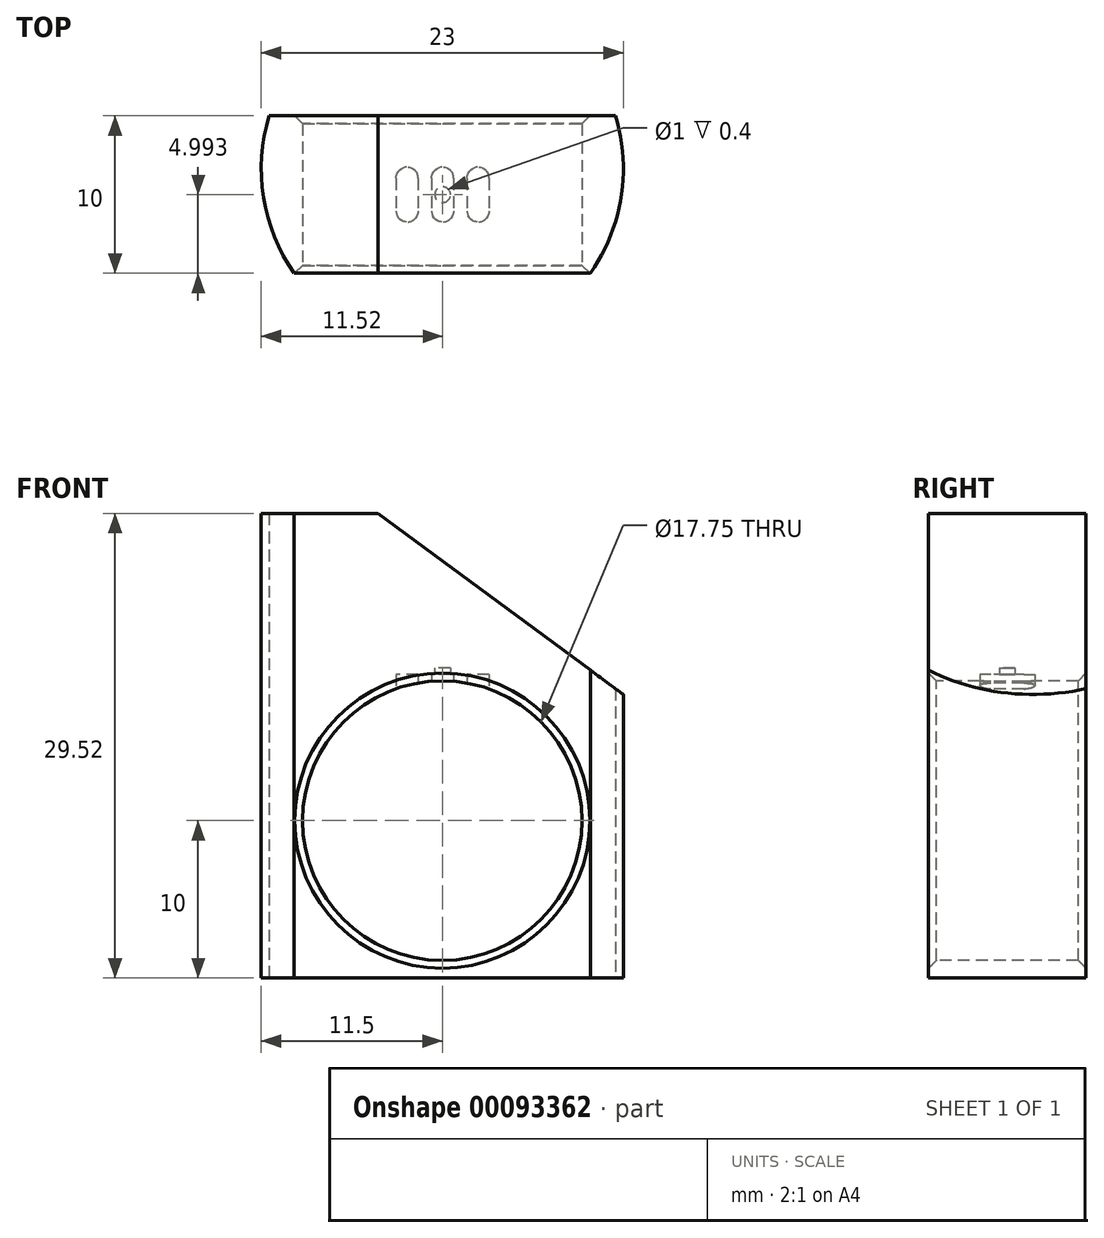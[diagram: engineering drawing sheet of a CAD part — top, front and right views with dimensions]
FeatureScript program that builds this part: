
annotation { "Feature Type Name" : "Feature", "Feature Type Description" : "" }
export const myFeature = defineFeature(function(context is Context, id is Id, definition is map)
    precondition{}
    {
        {
            var Q0;
            Q0=qCreatedBy(makeId("Front.planeOp"),FACE);
            var sketch = newSketch(context, id + "F0", { "sketchPlane" : qUnion([Q0])});
            skCircle(sketch, "E0", {"center": v(0, 0) * mm, "radius": 8.88 * mm});
            skSolve(sketch);
        }
        {
            var Q0;
            Q0=qCreatedBy(makeId("Top.planeOp"),FACE);
            var sketch = newSketch(context, id + "F1", { "sketchPlane" : qUnion([Q0])});
            skCircle(sketch, "E1", {"center": v(0, 0) * mm, "radius": 11.5 * mm});
            skSolve(sketch);
        }
        {
            var Q0;
            Q0=qSketchRegion(id+"F1",true);
            extrude(context, id + "F2", {"entities" : qUnion([Q0]), "depth" : 19.52 * mm, "hasSecondDirection" : true, "secondDirectionOppositeDirection" : true, "secondDirectionDepth" : 10 * mm});
        }
        {
            var Q0;
            Q0=qSketchRegion(id+"F0",true);
            extrude(context, id + "F3", {"entities" : qUnion([Q0]), "operationType" : NewBodyOperationType.REMOVE, "oppositeDirection" : true, "depth" : 25 * mm, "hasSecondDirection" : true, "secondDirectionOppositeDirection" : false, "secondDirectionDepth" : 25 * mm});
        }
        {
            var Q0;
            Q0=qCreatedBy(makeId("Front.planeOp"),FACE);
            var sketch = newSketch(context, id + "F4", { "sketchPlane" : qUnion([Q0])});
            skLineSegment(sketch, "E2", {"start": v(-16.33, 28.55) * mm, "end": v(24.77, -1.78) * mm});
            skLineSegment(sketch, "E3", {"start": v(24.77, -1.78) * mm, "end": v(24.77, 28.55) * mm});
            skLineSegment(sketch, "E4", {"start": v(24.77, 28.55) * mm, "end": v(-16.33, 28.55) * mm});
            skSolve(sketch);
        }
        {
            var Q0;
            Q0=qSketchRegion(id+"F4",true);
            extrude(context, id + "F5", {"entities" : qUnion([Q0]), "operationType" : NewBodyOperationType.REMOVE, "oppositeDirection" : true, "depth" : 25 * mm, "hasSecondDirection" : true, "secondDirectionOppositeDirection" : false, "secondDirectionDepth" : 25 * mm});
        }
        {
            var Q0;
            Q0=qCreatedBy(makeId("Top.planeOp"),FACE);
            var sketch = newSketch(context, id + "F6", { "sketchPlane" : qUnion([Q0])});
            skLineSegment(sketch, "E5.bottom", {"start": v(-13.62, -6.62) * mm, "end": v(17.44, -6.62) * mm});
            skLineSegment(sketch, "E5.top", {"start": v(-13.62, 3.38) * mm, "end": v(17.44, 3.38) * mm});
            skLineSegment(sketch, "E5.left", {"start": v(-13.62, -6.62) * mm, "end": v(-13.62, 3.38) * mm});
            skLineSegment(sketch, "E5.right", {"start": v(17.44, -6.62) * mm, "end": v(17.44, 3.38) * mm});
            skLineSegment(sketch, "E6", {"start": v(-13.62, 3.38) * mm, "end": v(-13.62, 17.25) * mm});
            skLineSegment(sketch, "E7", {"start": v(-13.62, 17.25) * mm, "end": v(17.44, 17.25) * mm});
            skLineSegment(sketch, "E8", {"start": v(17.44, 17.25) * mm, "end": v(17.44, 3.38) * mm});
            skLineSegment(sketch, "E9", {"start": v(-13.62, -6.62) * mm, "end": v(-13.62, -19.8) * mm});
            skLineSegment(sketch, "E10", {"start": v(-13.62, -19.8) * mm, "end": v(17.44, -19.8) * mm});
            skLineSegment(sketch, "E11", {"start": v(17.44, -19.8) * mm, "end": v(17.44, -6.62) * mm});
            skSolve(sketch);
        }
        {
            var Q0;
            Q0=makeQuery(id+"F6.imprint","IMPRINT",FACE,{"disambiguationData":[TD([[makeQuery(id+"F6.imprint","IMPRINT",EDGE,{"derivedFrom":sQuery(id+"F6.wireOp",EDGE,"E5.top")}),1.0]])]});
            var Q1;
            Q1=makeQuery(id+"F6.imprint","IMPRINT",FACE,{"disambiguationData":[TD([[makeQuery(id+"F6.imprint","IMPRINT",EDGE,{"derivedFrom":sQuery(id+"F6.wireOp",EDGE,"E5.bottom")}),-1.0]])]});
            extrude(context, id + "F7", {"entities" : qUnion([Q0, Q1]), "operationType" : NewBodyOperationType.REMOVE, "oppositeDirection" : true, "depth" : 25 * mm, "hasSecondDirection" : true, "secondDirectionOppositeDirection" : false, "secondDirectionDepth" : 25 * mm});
        }
        {
            var Q0;
            Q0=makeQuery(id+"F7.boolean.opBoolean","INTERSECT",EDGE,{"derivedFrom":[makeQuery(id+"F3.boolean.opBoolean","COPY",FACE,{"derivedFrom":makeQuery(id+"F3.opExtrude","SWEPT_FACE",FACE,{"disambiguationData":[OSD([sQuery(id+"F0.wireOp",EDGE,"E0")])]})}),makeQuery(id+"F7.opExtrude","SWEPT_FACE",FACE,{"disambiguationData":[OSD([sQuery(id+"F6.wireOp",EDGE,"E5.top")])]})]});
            var Q1;
            Q1=makeQuery(id+"F7.boolean.opBoolean","INTERSECT",EDGE,{"derivedFrom":[makeQuery(id+"F3.boolean.opBoolean","COPY",FACE,{"derivedFrom":makeQuery(id+"F3.opExtrude","SWEPT_FACE",FACE,{"disambiguationData":[OSD([sQuery(id+"F0.wireOp",EDGE,"E0")])]})}),makeQuery(id+"F7.opExtrude","SWEPT_FACE",FACE,{"disambiguationData":[OSD([sQuery(id+"F6.wireOp",EDGE,"E5.bottom")])]})]});
            chamfer(context, id + "F8", {"entities" : qUnion([Q0, Q1]), "width" : .5 * mm, "tangentPropagation" : true});
        }
        {
            var Q0;
            Q0=qCreatedBy(makeId("Top.planeOp"),FACE);
            var sketch = newSketch(context, id + "F9", { "sketchPlane" : qUnion([Q0])});
            skLineSegment(sketch, "E12.bottom", {"start": v(-0.68, -0.58) * mm, "end": v(-0.68, -2.67) * mm});
            skArc(sketch, "E13.filletArc", {"start": v(0.72, -0.58) * mm, "mid": v(0.52, -0.08) * mm, "end": v(0.02, 0.12) * mm});
            skArc(sketch, "E14.filletArc", {"start": v(0.02, 0.12) * mm, "mid": v(-0.47, -0.08) * mm, "end": v(-0.68, -0.58) * mm});
            skArc(sketch, "E15.filletArc", {"start": v(0.02, -3.37) * mm, "mid": v(0.52, -3.16) * mm, "end": v(0.72, -2.67) * mm});
            skArc(sketch, "E16.filletArc", {"start": v(-0.68, -2.67) * mm, "mid": v(-0.47, -3.16) * mm, "end": v(0.02, -3.37) * mm});
            skLineSegment(sketch, "E17.bottom", {"start": v(-2.93, -0.58) * mm, "end": v(-2.93, -2.67) * mm});
            skLineSegment(sketch, "E17.top", {"start": v(-1.53, -0.58) * mm, "end": v(-1.53, -2.67) * mm});
            skArc(sketch, "E18.filletArc", {"start": v(-1.53, -0.58) * mm, "mid": v(-1.74, -0.08) * mm, "end": v(-2.23, 0.12) * mm});
            skArc(sketch, "E19.filletArc", {"start": v(-2.23, 0.12) * mm, "mid": v(-2.73, -0.08) * mm, "end": v(-2.93, -0.58) * mm});
            skArc(sketch, "E20.filletArc", {"start": v(-2.23, -3.37) * mm, "mid": v(-1.74, -3.16) * mm, "end": v(-1.53, -2.67) * mm});
            skArc(sketch, "E21.filletArc", {"start": v(-2.93, -2.67) * mm, "mid": v(-2.73, -3.16) * mm, "end": v(-2.23, -3.37) * mm});
            skLineSegment(sketch, "E22", {"start": v(0.72, -0.58) * mm, "end": v(0.72, -2.67) * mm});
            skCircle(sketch, "E23", {"center": v(0.02, -1.63) * mm, "radius": 0.5 * mm});
            skLineSegment(sketch, "E24.bottom", {"start": v(1.58, -0.58) * mm, "end": v(1.58, -2.67) * mm});
            skLineSegment(sketch, "E24.top", {"start": v(2.98, -0.58) * mm, "end": v(2.98, -2.67) * mm});
            skArc(sketch, "E25.filletArc", {"start": v(2.98, -0.58) * mm, "mid": v(2.77, -0.08) * mm, "end": v(2.28, 0.12) * mm});
            skArc(sketch, "E26.filletArc", {"start": v(2.28, 0.12) * mm, "mid": v(1.78, -0.08) * mm, "end": v(1.58, -0.58) * mm});
            skArc(sketch, "E27.filletArc", {"start": v(2.28, -3.37) * mm, "mid": v(2.77, -3.16) * mm, "end": v(2.98, -2.67) * mm});
            skArc(sketch, "E28.filletArc", {"start": v(1.58, -2.67) * mm, "mid": v(1.78, -3.16) * mm, "end": v(2.28, -3.37) * mm});
            skPoint(sketch, "E29", {"position": v(0, 3.38) * mm});
            skPoint(sketch, "E30", {"position": v(0.02, -6.64) * mm});
            skSolve(sketch);
        }
        {
            var Q0;
            Q0=makeQuery(id+"F9.imprint","IMPRINT",FACE,{"disambiguationData":[TD([[makeQuery(id+"F9.imprint","IMPRINT",EDGE,{"derivedFrom":sQuery(id+"F9.wireOp",EDGE,"E17.bottom")}),1.0]])]});
            var Q1;
            Q1=makeQuery(id+"F9.imprint","IMPRINT",FACE,{"disambiguationData":[TD([[makeQuery(id+"F9.imprint","IMPRINT",EDGE,{"derivedFrom":sQuery(id+"F9.wireOp",EDGE,"E12.bottom")}),1.0]])]});
            var Q2;
            Q2=makeQuery(id+"F9.imprint","IMPRINT",FACE,{"disambiguationData":[TD([[makeQuery(id+"F9.imprint","IMPRINT",EDGE,{"derivedFrom":sQuery(id+"F9.wireOp",EDGE,"E24.bottom")}),1.0]])]});
            extrude(context, id + "F10", {"entities" : qUnion([Q0, Q1, Q2]), "operationType" : NewBodyOperationType.REMOVE, "depth" : 9.3 * mm});
        }
        {
            var Q0;
            Q0=makeQuery(id+"F9.imprint","IMPRINT",FACE,{"disambiguationData":[TD([[makeQuery(id+"F9.imprint","IMPRINT",EDGE,{"derivedFrom":sQuery(id+"F9.wireOp",EDGE,"E23")}),1.0]])]});
            extrude(context, id + "F11", {"entities" : qUnion([Q0]), "operationType" : NewBodyOperationType.REMOVE, "depth" : 9.7 * mm});
        }
    });
